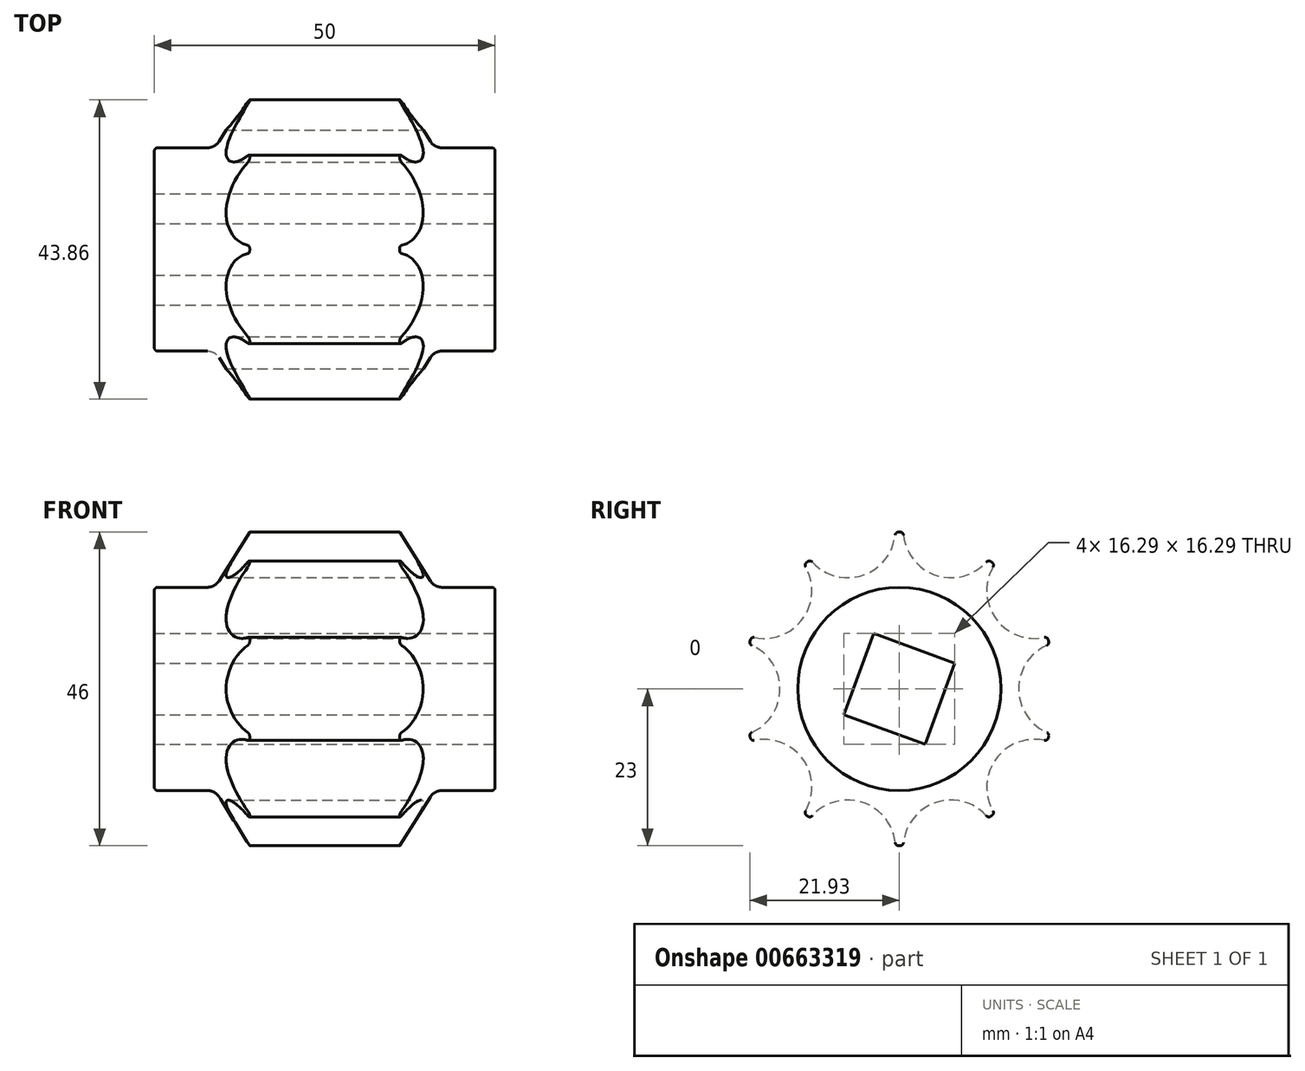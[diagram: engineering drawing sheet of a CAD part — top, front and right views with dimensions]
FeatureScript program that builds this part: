
annotation { "Feature Type Name" : "Feature", "Feature Type Description" : "" }
export const myFeature = defineFeature(function(context is Context, id is Id, definition is map)
    precondition{}
    {
        {
            var Q0;
            Q0=qCreatedBy(makeId("Front.planeOp"),FACE);
            var sketch = newSketch(context, id + "F0", { "sketchPlane" : qUnion([Q0])});
            skLineSegment(sketch, "E0", {"start": v(25, 5) * mm, "end": v(25, 14.9) * mm});
            skLineSegment(sketch, "E1", {"start": v(25, 14.9) * mm, "end": v(16.1, 14.9) * mm});
            skLineSegment(sketch, "E2", {"start": v(11, 23) * mm, "end": v(-11, 23) * mm});
            skLineSegment(sketch, "E3", {"start": v(-25, 14.9) * mm, "end": v(-25, 5) * mm});
            skLineSegment(sketch, "E4", {"start": v(-25, 5) * mm, "end": v(25, 5) * mm});
            skPoint(sketch, "E5.start.orphan", {"position": v(-25, 0) * mm});
            skLineSegment(sketch, "E6", {"start": v(-25, 0) * mm, "end": v(30.22, 0) * mm, "construction": true});
            skLineSegment(sketch, "E7", {"start": v(11, 23) * mm, "end": v(16.1, 14.9) * mm});
            skLineSegment(sketch, "E8", {"start": v(-25, 14.9) * mm, "end": v(-16.1, 14.9) * mm});
            skLineSegment(sketch, "E9", {"start": v(-16.1, 14.9) * mm, "end": v(-11, 23) * mm});
            skSolve(sketch);
        }
        {
            var Q0;
            Q0=makeQuery(id+"F0.imprint","IMPRINT",FACE,{"disambiguationData":[TD([[makeQuery(id+"F0.imprint","IMPRINT",EDGE,{"derivedFrom":sQuery(id+"F0.wireOp",EDGE,"E0")}),1.0]])]});
            var Q1;
            Q1=sQuery(id+"F0.wireOp",EDGE,"E6");
            revolve(context, id + "F1", {"entities" : qUnion([Q0]), "axis" : qUnion([Q1]), "revolveType" : RevolveType.FULL});
        }
        {
            var Q0;
            Q0=makeQuery(id+"F1.opRevolve","SWEPT_FACE",FACE,{"disambiguationData":[OSD([sQuery(id+"F0.wireOp",EDGE,"E0")])]});
            var sketch = newSketch(context, id + "F2", { "sketchPlane" : qUnion([Q0])});
            skCircle(sketch, "E10.cCircle", {"center": v(0, 0) * mm, "radius": 6.35 * mm, "construction": true});
            skLineSegment(sketch, "E10.0", {"start": v(8.14, 3.79) * mm, "end": v(3.79, -8.14) * mm});
            skLineSegment(sketch, "E10.1", {"start": v(3.79, -8.14) * mm, "end": v(-8.14, -3.79) * mm});
            skLineSegment(sketch, "E10.2", {"start": v(-8.14, -3.79) * mm, "end": v(-3.79, 8.14) * mm});
            skLineSegment(sketch, "E10.3", {"start": v(-3.79, 8.14) * mm, "end": v(8.14, 3.79) * mm});
            skPoint(sketch, "E10.0.midPoint", {"position": v(5.96, -2.18) * mm});
            skCircle(sketch, "E11", {"center": v(24.5, 0) * mm, "radius": 7 * mm});
            skCircle(sketch, "E12.1.0", {"center": v(19.82, 14.4) * mm, "radius": 7 * mm});
            skCircle(sketch, "E12.2.0", {"center": v(7.57, 23.3) * mm, "radius": 7 * mm});
            skCircle(sketch, "E12.3.0", {"center": v(-7.57, 23.3) * mm, "radius": 7 * mm});
            skCircle(sketch, "E12.4.0", {"center": v(-19.82, 14.4) * mm, "radius": 7 * mm});
            skCircle(sketch, "E12.5.0", {"center": v(-24.5, 0) * mm, "radius": 7 * mm});
            skCircle(sketch, "E12.6.0", {"center": v(-19.82, -14.4) * mm, "radius": 7 * mm});
            skCircle(sketch, "E12.7.0", {"center": v(-7.57, -23.3) * mm, "radius": 7 * mm});
            skCircle(sketch, "E12.8.0", {"center": v(7.57, -23.3) * mm, "radius": 7 * mm});
            skCircle(sketch, "E12.9.0", {"center": v(19.82, -14.4) * mm, "radius": 7 * mm});
            skSolve(sketch);
        }
        {
            var Q0;
            Q0=makeQuery(id+"F1.opRevolve","SWEPT_EDGE",EDGE,{"disambiguationData":[OSD([sQuery(id+"F0.wireOp",EDGE,"E3"),sQuery(id+"F0.wireOp",EDGE,"E8")])]});
            var Q1;
            Q1=makeQuery(id+"F1.opRevolve","SWEPT_EDGE",EDGE,{"disambiguationData":[OSD([sQuery(id+"F0.wireOp",EDGE,"E0"),sQuery(id+"F0.wireOp",EDGE,"E1")])]});
            fillet(context, id + "F3", {"entities" : qUnion([Q0, Q1]), "radius" : .5 * mm, "tangentPropagation" : true, "allowEdgeOverflow" : false});
        }
        {
            var Q0;
            Q0=makeQuery(id+"F2.imprint","IMPRINT",FACE,{"disambiguationData":[TD([[makeQuery(id+"F2.imprint","IMPRINT",EDGE,{"derivedFrom":sQuery(id+"F2.wireOp",EDGE,"E10.0")}),-1.0]])]});
            extrude(context, id + "F4", {"entities" : qUnion([Q0]), "operationType" : NewBodyOperationType.REMOVE, "oppositeDirection" : true, "depth" : 50 * mm, "offsetDistance" : 25 * mm});
        }
        {
            var Q0;
            Q0=makeQuery(id+"F2.imprint","IMPRINT",FACE,{"disambiguationData":[TD([[makeQuery(id+"F2.imprint","IMPRINT",EDGE,{"derivedFrom":sQuery(id+"F2.wireOp",EDGE,"E12.1.0")}),1.0]])]});
            var Q1;
            Q1=makeQuery(id+"F2.imprint","IMPRINT",FACE,{"disambiguationData":[TD([[makeQuery(id+"F2.imprint","IMPRINT",EDGE,{"derivedFrom":sQuery(id+"F2.wireOp",EDGE,"E11")}),1.0]])]});
            var Q2;
            Q2=makeQuery(id+"F2.imprint","IMPRINT",FACE,{"disambiguationData":[TD([[makeQuery(id+"F2.imprint","IMPRINT",EDGE,{"derivedFrom":sQuery(id+"F2.wireOp",EDGE,"E12.9.0")}),1.0]])]});
            var Q3;
            Q3=makeQuery(id+"F2.imprint","IMPRINT",FACE,{"disambiguationData":[TD([[makeQuery(id+"F2.imprint","IMPRINT",EDGE,{"derivedFrom":sQuery(id+"F2.wireOp",EDGE,"E12.8.0")}),1.0]])]});
            var Q4;
            Q4=makeQuery(id+"F2.imprint","IMPRINT",FACE,{"disambiguationData":[TD([[makeQuery(id+"F2.imprint","IMPRINT",EDGE,{"derivedFrom":sQuery(id+"F2.wireOp",EDGE,"E12.7.0")}),1.0]])]});
            var Q5;
            Q5=makeQuery(id+"F2.imprint","IMPRINT",FACE,{"disambiguationData":[TD([[makeQuery(id+"F2.imprint","IMPRINT",EDGE,{"derivedFrom":sQuery(id+"F2.wireOp",EDGE,"E12.6.0")}),1.0]])]});
            var Q6;
            Q6=makeQuery(id+"F2.imprint","IMPRINT",FACE,{"disambiguationData":[TD([[makeQuery(id+"F2.imprint","IMPRINT",EDGE,{"derivedFrom":sQuery(id+"F2.wireOp",EDGE,"E12.5.0")}),1.0]])]});
            var Q7;
            Q7=makeQuery(id+"F2.imprint","IMPRINT",FACE,{"disambiguationData":[TD([[makeQuery(id+"F2.imprint","IMPRINT",EDGE,{"derivedFrom":sQuery(id+"F2.wireOp",EDGE,"E12.3.0")}),1.0]])]});
            var Q8;
            Q8=makeQuery(id+"F2.imprint","IMPRINT",FACE,{"disambiguationData":[TD([[makeQuery(id+"F2.imprint","IMPRINT",EDGE,{"derivedFrom":sQuery(id+"F2.wireOp",EDGE,"E12.2.0")}),1.0]])]});
            var Q9;
            Q9=makeQuery(id+"F2.imprint","IMPRINT",FACE,{"disambiguationData":[TD([[makeQuery(id+"F2.imprint","IMPRINT",EDGE,{"derivedFrom":sQuery(id+"F2.wireOp",EDGE,"E12.4.0")}),1.0]])]});
            extrude(context, id + "F5", {"entities" : qUnion([Q0, Q1, Q2, Q3, Q4, Q5, Q6, Q7, Q8, Q9]), "operationType" : NewBodyOperationType.REMOVE, "oppositeDirection" : true, "depth" : 50 * mm});
        }
        {
            var Q0;
            Q0=makeQuery(id+"F1.opRevolve","SWEPT_EDGE",EDGE,{"disambiguationData":[OSD([sQuery(id+"F0.wireOp",EDGE,"E1"),sQuery(id+"F0.wireOp",EDGE,"lQtPVyIY-ggqZ-GcBV-1edM-0pXQkhYFdYdI")])]});
            var Q1;
            Q1=makeQuery(id+"F1.opRevolve","SWEPT_EDGE",EDGE,{"disambiguationData":[OSD([sQuery(id+"F0.wireOp",EDGE,"0TzLTUSK-P1le-NMfB-YZgS-nyDzrUtxSBo3"),sQuery(id+"F0.wireOp",EDGE,"mhRDrD4P-eXcN-jgfk-grpd-L3LYcjMJo5U6")])]});
            fillet(context, id + "F6", {"entities" : qUnion([Q0, Q1]), "radius" : 2 * mm, "tangentPropagation" : true, "allowEdgeOverflow" : false});
        }
        {
            var Q0;
            Q0=makeQuery(id+"F5.boolean.opBoolean","INTERSECT",EDGE,{"disambiguationData":[OD(1.0)],"derivedFrom":[makeQuery(id+"F1.opRevolve","SWEPT_FACE",FACE,{"disambiguationData":[OSD([sQuery(id+"F0.wireOp",EDGE,"E2")])]}),makeQuery(id+"F5.opExtrude","SWEPT_FACE",FACE,{"disambiguationData":[OSD([sQuery(id+"F2.wireOp",EDGE,"E12.2.0")])]})]});
            var Q1;
            Q1=makeQuery(id+"F5.boolean.opBoolean","INTERSECT",EDGE,{"disambiguationData":[OD(0.0)],"derivedFrom":[makeQuery(id+"F1.opRevolve","SWEPT_FACE",FACE,{"disambiguationData":[OSD([sQuery(id+"F0.wireOp",EDGE,"E2")])]}),makeQuery(id+"F5.opExtrude","SWEPT_FACE",FACE,{"disambiguationData":[OSD([sQuery(id+"F2.wireOp",EDGE,"E12.3.0")])]})]});
            var Q2;
            Q2=makeQuery(id+"F5.boolean.opBoolean","INTERSECT",EDGE,{"disambiguationData":[OD(0.0)],"derivedFrom":[makeQuery(id+"F1.opRevolve","SWEPT_FACE",FACE,{"disambiguationData":[OSD([sQuery(id+"F0.wireOp",EDGE,"E2")])]}),makeQuery(id+"F5.opExtrude","SWEPT_FACE",FACE,{"disambiguationData":[OSD([sQuery(id+"F2.wireOp",EDGE,"E12.2.0")])]})]});
            var Q3;
            Q3=makeQuery(id+"F5.boolean.opBoolean","INTERSECT",EDGE,{"disambiguationData":[OD(1.0)],"derivedFrom":[makeQuery(id+"F1.opRevolve","SWEPT_FACE",FACE,{"disambiguationData":[OSD([sQuery(id+"F0.wireOp",EDGE,"E2")])]}),makeQuery(id+"F5.opExtrude","SWEPT_FACE",FACE,{"disambiguationData":[OSD([sQuery(id+"F2.wireOp",EDGE,"E12.1.0")])]})]});
            var Q4;
            Q4=makeQuery(id+"F5.boolean.opBoolean","INTERSECT",EDGE,{"disambiguationData":[OD(0.0)],"derivedFrom":[makeQuery(id+"F1.opRevolve","SWEPT_FACE",FACE,{"disambiguationData":[OSD([sQuery(id+"F0.wireOp",EDGE,"E2")])]}),makeQuery(id+"F5.opExtrude","SWEPT_FACE",FACE,{"disambiguationData":[OSD([sQuery(id+"F2.wireOp",EDGE,"E12.1.0")])]})]});
            var Q5;
            Q5=makeQuery(id+"F5.boolean.opBoolean","INTERSECT",EDGE,{"disambiguationData":[OD(0.0)],"derivedFrom":[makeQuery(id+"F1.opRevolve","SWEPT_FACE",FACE,{"disambiguationData":[OSD([sQuery(id+"F0.wireOp",EDGE,"E2")])]}),makeQuery(id+"F5.opExtrude","SWEPT_FACE",FACE,{"disambiguationData":[OSD([sQuery(id+"F2.wireOp",EDGE,"E11")])]})]});
            var Q6;
            Q6=makeQuery(id+"F5.boolean.opBoolean","INTERSECT",EDGE,{"disambiguationData":[OD(1.0)],"derivedFrom":[makeQuery(id+"F1.opRevolve","SWEPT_FACE",FACE,{"disambiguationData":[OSD([sQuery(id+"F0.wireOp",EDGE,"E2")])]}),makeQuery(id+"F5.opExtrude","SWEPT_FACE",FACE,{"disambiguationData":[OSD([sQuery(id+"F2.wireOp",EDGE,"E11")])]})]});
            var Q7;
            Q7=makeQuery(id+"F5.boolean.opBoolean","INTERSECT",EDGE,{"disambiguationData":[OD(0.0)],"derivedFrom":[makeQuery(id+"F1.opRevolve","SWEPT_FACE",FACE,{"disambiguationData":[OSD([sQuery(id+"F0.wireOp",EDGE,"E2")])]}),makeQuery(id+"F5.opExtrude","SWEPT_FACE",FACE,{"disambiguationData":[OSD([sQuery(id+"F2.wireOp",EDGE,"E12.9.0")])]})]});
            var Q8;
            Q8=makeQuery(id+"F5.boolean.opBoolean","INTERSECT",EDGE,{"disambiguationData":[OD(1.0)],"derivedFrom":[makeQuery(id+"F1.opRevolve","SWEPT_FACE",FACE,{"disambiguationData":[OSD([sQuery(id+"F0.wireOp",EDGE,"E2")])]}),makeQuery(id+"F5.opExtrude","SWEPT_FACE",FACE,{"disambiguationData":[OSD([sQuery(id+"F2.wireOp",EDGE,"E12.9.0")])]})]});
            var Q9;
            Q9=makeQuery(id+"F5.boolean.opBoolean","INTERSECT",EDGE,{"disambiguationData":[OD(1.0)],"derivedFrom":[makeQuery(id+"F1.opRevolve","SWEPT_FACE",FACE,{"disambiguationData":[OSD([sQuery(id+"F0.wireOp",EDGE,"E2")])]}),makeQuery(id+"F5.opExtrude","SWEPT_FACE",FACE,{"disambiguationData":[OSD([sQuery(id+"F2.wireOp",EDGE,"E12.8.0")])]})]});
            var Q10;
            Q10=makeQuery(id+"F5.boolean.opBoolean","INTERSECT",EDGE,{"disambiguationData":[OD(0.0)],"derivedFrom":[makeQuery(id+"F1.opRevolve","SWEPT_FACE",FACE,{"disambiguationData":[OSD([sQuery(id+"F0.wireOp",EDGE,"E2")])]}),makeQuery(id+"F5.opExtrude","SWEPT_FACE",FACE,{"disambiguationData":[OSD([sQuery(id+"F2.wireOp",EDGE,"E12.8.0")])]})]});
            var Q11;
            Q11=makeQuery(id+"F5.boolean.opBoolean","INTERSECT",EDGE,{"disambiguationData":[OD(1.0)],"derivedFrom":[makeQuery(id+"F1.opRevolve","SWEPT_FACE",FACE,{"disambiguationData":[OSD([sQuery(id+"F0.wireOp",EDGE,"E2")])]}),makeQuery(id+"F5.opExtrude","SWEPT_FACE",FACE,{"disambiguationData":[OSD([sQuery(id+"F2.wireOp",EDGE,"E12.7.0")])]})]});
            var Q12;
            Q12=makeQuery(id+"F5.boolean.opBoolean","INTERSECT",EDGE,{"disambiguationData":[OD(0.0)],"derivedFrom":[makeQuery(id+"F1.opRevolve","SWEPT_FACE",FACE,{"disambiguationData":[OSD([sQuery(id+"F0.wireOp",EDGE,"E2")])]}),makeQuery(id+"F5.opExtrude","SWEPT_FACE",FACE,{"disambiguationData":[OSD([sQuery(id+"F2.wireOp",EDGE,"E12.7.0")])]})]});
            var Q13;
            Q13=makeQuery(id+"F5.boolean.opBoolean","INTERSECT",EDGE,{"disambiguationData":[OD(1.0)],"derivedFrom":[makeQuery(id+"F1.opRevolve","SWEPT_FACE",FACE,{"disambiguationData":[OSD([sQuery(id+"F0.wireOp",EDGE,"E2")])]}),makeQuery(id+"F5.opExtrude","SWEPT_FACE",FACE,{"disambiguationData":[OSD([sQuery(id+"F2.wireOp",EDGE,"E12.6.0")])]})]});
            var Q14;
            Q14=makeQuery(id+"F5.boolean.opBoolean","INTERSECT",EDGE,{"disambiguationData":[OD(0.0)],"derivedFrom":[makeQuery(id+"F1.opRevolve","SWEPT_FACE",FACE,{"disambiguationData":[OSD([sQuery(id+"F0.wireOp",EDGE,"E2")])]}),makeQuery(id+"F5.opExtrude","SWEPT_FACE",FACE,{"disambiguationData":[OSD([sQuery(id+"F2.wireOp",EDGE,"E12.6.0")])]})]});
            var Q15;
            Q15=makeQuery(id+"F5.boolean.opBoolean","INTERSECT",EDGE,{"disambiguationData":[OD(1.0)],"derivedFrom":[makeQuery(id+"F1.opRevolve","SWEPT_FACE",FACE,{"disambiguationData":[OSD([sQuery(id+"F0.wireOp",EDGE,"E2")])]}),makeQuery(id+"F5.opExtrude","SWEPT_FACE",FACE,{"disambiguationData":[OSD([sQuery(id+"F2.wireOp",EDGE,"E12.5.0")])]})]});
            var Q16;
            Q16=makeQuery(id+"F5.boolean.opBoolean","INTERSECT",EDGE,{"disambiguationData":[OD(0.0)],"derivedFrom":[makeQuery(id+"F1.opRevolve","SWEPT_FACE",FACE,{"disambiguationData":[OSD([sQuery(id+"F0.wireOp",EDGE,"E2")])]}),makeQuery(id+"F5.opExtrude","SWEPT_FACE",FACE,{"disambiguationData":[OSD([sQuery(id+"F2.wireOp",EDGE,"E12.5.0")])]})]});
            var Q17;
            Q17=makeQuery(id+"F5.boolean.opBoolean","INTERSECT",EDGE,{"disambiguationData":[OD(1.0)],"derivedFrom":[makeQuery(id+"F1.opRevolve","SWEPT_FACE",FACE,{"disambiguationData":[OSD([sQuery(id+"F0.wireOp",EDGE,"E2")])]}),makeQuery(id+"F5.opExtrude","SWEPT_FACE",FACE,{"disambiguationData":[OSD([sQuery(id+"F2.wireOp",EDGE,"E12.4.0")])]})]});
            var Q18;
            Q18=makeQuery(id+"F5.boolean.opBoolean","INTERSECT",EDGE,{"disambiguationData":[OD(0.0)],"derivedFrom":[makeQuery(id+"F1.opRevolve","SWEPT_FACE",FACE,{"disambiguationData":[OSD([sQuery(id+"F0.wireOp",EDGE,"E2")])]}),makeQuery(id+"F5.opExtrude","SWEPT_FACE",FACE,{"disambiguationData":[OSD([sQuery(id+"F2.wireOp",EDGE,"E12.4.0")])]})]});
            var Q19;
            Q19=makeQuery(id+"F5.boolean.opBoolean","INTERSECT",EDGE,{"disambiguationData":[OD(1.0)],"derivedFrom":[makeQuery(id+"F1.opRevolve","SWEPT_FACE",FACE,{"disambiguationData":[OSD([sQuery(id+"F0.wireOp",EDGE,"E2")])]}),makeQuery(id+"F5.opExtrude","SWEPT_FACE",FACE,{"disambiguationData":[OSD([sQuery(id+"F2.wireOp",EDGE,"E12.3.0")])]})]});
            fillet(context, id + "F7", {"entities" : qUnion([Q0, Q1, Q2, Q3, Q4, Q5, Q6, Q7, Q8, Q9, Q10, Q11, Q12, Q13, Q14, Q15, Q16, Q17, Q18, Q19]), "radius" : .5 * mm, "tangentPropagation" : true, "allowEdgeOverflow" : false});
        }
        {
            var Q0;
            Q0=makeQuery(id+"F1.opRevolve","SWEPT_EDGE",EDGE,{"disambiguationData":[OSD([sQuery(id+"F0.wireOp",EDGE,"E8"),sQuery(id+"F0.wireOp",EDGE,"E9")])]});
            fillet(context, id + "F8", {"entities" : qUnion([Q0]), "radius" : 2 * mm, "tangentPropagation" : true, "allowEdgeOverflow" : false});
        }
        {
            var Q0;
            Q0=makeQuery(id+"F1.opRevolve","SWEPT_BODY",BODY,{"disambiguationData":[OSD([sQuery(id+"F0.wireOp",EDGE,"E0"),sQuery(id+"F0.wireOp",EDGE,"E1"),sQuery(id+"F0.wireOp",EDGE,"E2"),sQuery(id+"F0.wireOp",EDGE,"E3"),sQuery(id+"F0.wireOp",EDGE,"E4"),sQuery(id+"F0.wireOp",EDGE,"E7"),sQuery(id+"F0.wireOp",EDGE,"E8"),sQuery(id+"F0.wireOp",EDGE,"E9")])]});
            transform(context, id + "F9", {"entities" : qUnion([Q0]), "transformType" : TransformType.TRANSLATION_3D, "dx" : 0 * mm, "dy" : 71.6 * mm, "dz" : 0 * mm, "makeCopy" : true});
        }
        {
            var Q0;
            Q0=makeQuery(id+"F9.opPattern","COPY",BODY,{"derivedFrom":makeQuery(id+"F1.opRevolve","SWEPT_BODY",BODY,{"disambiguationData":[OSD([sQuery(id+"F0.wireOp",EDGE,"E0"),sQuery(id+"F0.wireOp",EDGE,"E1"),sQuery(id+"F0.wireOp",EDGE,"E2"),sQuery(id+"F0.wireOp",EDGE,"E3"),sQuery(id+"F0.wireOp",EDGE,"E4"),sQuery(id+"F0.wireOp",EDGE,"E7"),sQuery(id+"F0.wireOp",EDGE,"E8"),sQuery(id+"F0.wireOp",EDGE,"E9")])]}),"instanceName":"1"});
            deleteBodies(context, id + "F10", {"entities" : qUnion([Q0])});
        }
    });
